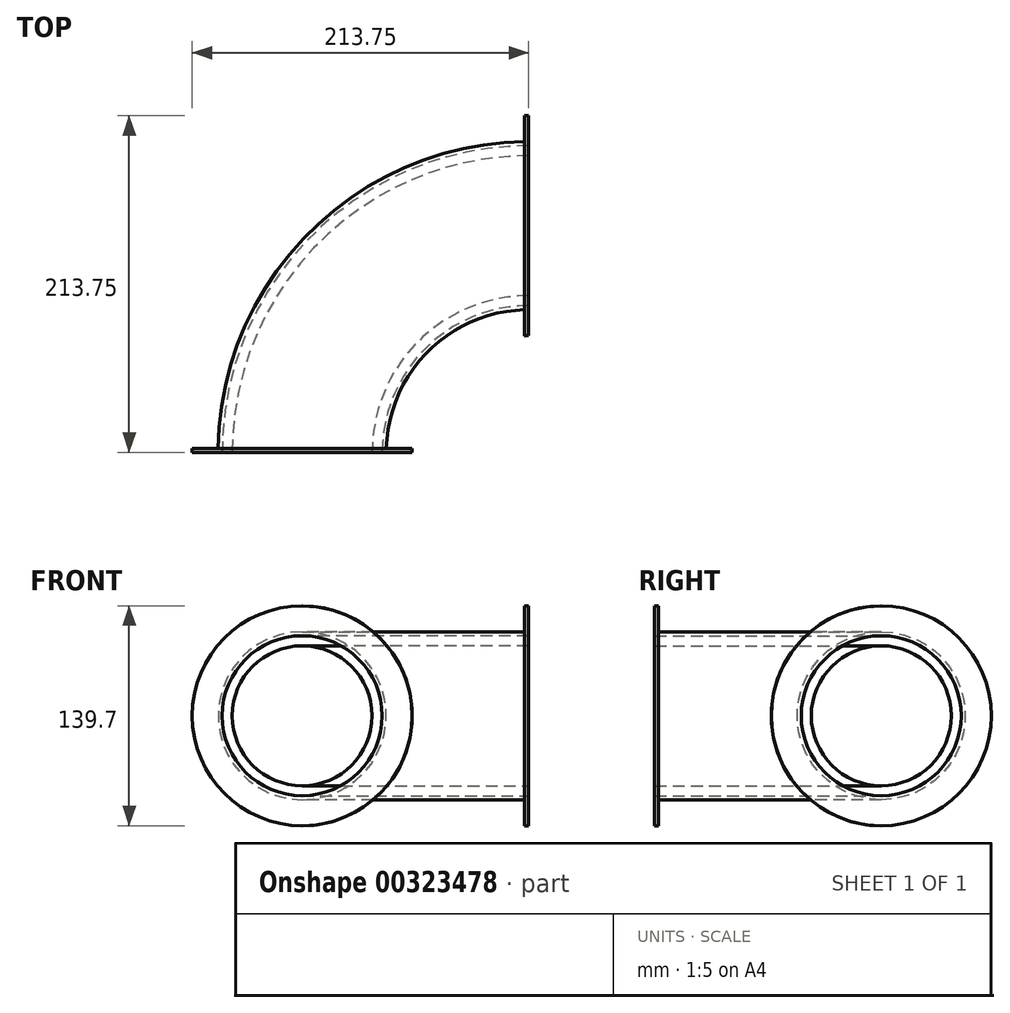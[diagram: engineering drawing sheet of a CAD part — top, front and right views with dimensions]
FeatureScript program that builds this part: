
annotation { "Feature Type Name" : "Feature", "Feature Type Description" : "" }
export const myFeature = defineFeature(function(context is Context, id is Id, definition is map)
    precondition{}
    {
        {
            var Q0;
            Q0=qCreatedBy(makeId("Top.planeOp"),FACE);
            var sketch = newSketch(context, id + "F0", { "sketchPlane" : qUnion([Q0])});
            skArc(sketch, "E0", {"start": v(-57.4, 0) * mm, "mid": v(-40.59, 40.59) * mm, "end": v(0, 57.4) * mm});
            skSolve(sketch);
        }
        {
            var Q0;
            Q0=qCreatedBy(makeId("Front.planeOp"),FACE);
            var sketch = newSketch(context, id + "F1", { "sketchPlane" : qUnion([Q0])});
            skCircle(sketch, "E1", {"center": v(-143.9, 0) * mm, "radius": 50.8 * mm});
            skCircle(sketch, "E2", {"center": v(-143.9, 0) * mm, "radius": 44.45 * mm});
            skCircle(sketch, "E3", {"center": v(-143.9, 0) * mm, "radius": 69.85 * mm});
            skSolve(sketch);
        }
        {
            var Q0;
            Q0=makeQuery(id+"F1.imprint","IMPRINT",FACE,{"disambiguationData":[TD([[makeQuery(id+"F1.imprint","IMPRINT",EDGE,{"derivedFrom":sQuery(id+"F1.wireOp",EDGE,"E2")}),1.0]])]});
            var Q1;
            Q1=makeQuery(id+"F1.imprint","IMPRINT",FACE,{"disambiguationData":[TD([[makeQuery(id+"F1.imprint","IMPRINT",EDGE,{"derivedFrom":sQuery(id+"F1.wireOp",EDGE,"E1")}),-1.0]])]});
            var Q2;
            Q2=sQuery(id+"F0.wireOp",EDGE,"E0");
            sweep(context, id + "F2", {"profiles" : qUnion([Q0, Q1]), "path" : qUnion([Q2])});
        }
        {
            var Q0;
            Q0=makeQuery(id+"F2.opSweep","SWEPT_FACE",FACE,{"disambiguationData":[OSD([sQuery(id+"F0.wireOp",EDGE,"E0"),sQuery(id+"F1.wireOp",EDGE,"E3")])]});
            shell(context, id + "F3", {"entities" : qUnion([Q0]), "thickness" : 2.54 * mm});
        }
    });
